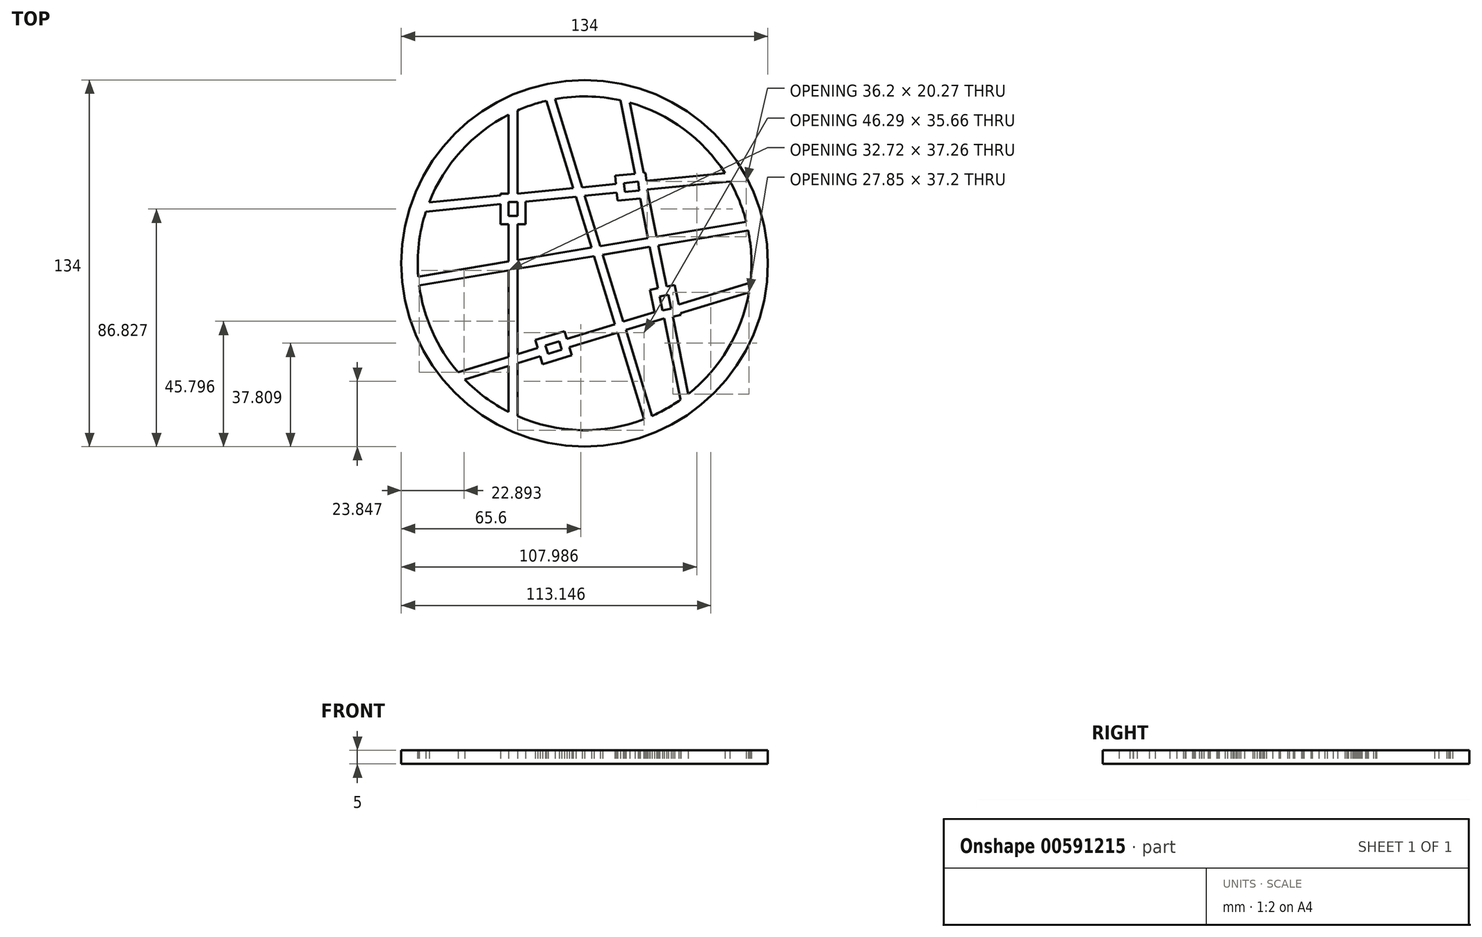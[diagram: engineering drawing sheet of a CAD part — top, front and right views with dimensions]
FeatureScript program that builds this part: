
annotation { "Feature Type Name" : "Feature", "Feature Type Description" : "" }
export const myFeature = defineFeature(function(context is Context, id is Id, definition is map)
    precondition{}
    {
        {
            var Q0;
            Q0=qCreatedBy(makeId("Top.planeOp"),FACE);
            var sketch = newSketch(context, id + "F0", { "sketchPlane" : qUnion([Q0])});
            skCircle(sketch, "E0", {"center": v(0, 0) * mm, "radius": 67 * mm});
            skArc(sketch, "E1.0", {"start": v(51.3, 33) * mm, "mid": v(36.26, 49.05) * mm, "end": v(16.5, 58.73) * mm});
            skLineSegment(sketch, "E2.bottom", {"start": v(-27.75, 22.47) * mm, "end": v(-24.55, 22.47) * mm});
            skLineSegment(sketch, "E2.top", {"start": v(-27.75, 17.27) * mm, "end": v(-24.55, 17.27) * mm});
            skLineSegment(sketch, "E2.left", {"start": v(-27.75, 22.47) * mm, "end": v(-27.75, 17.27) * mm});
            skLineSegment(sketch, "E2.right", {"start": v(-24.55, 22.47) * mm, "end": v(-24.55, 17.27) * mm});
            skLineSegment(sketch, "E3.1.0", {"start": v(19.92, 26.65) * mm, "end": v(14.75, 26.14) * mm});
            skLineSegment(sketch, "E3.1.1", {"start": v(19.6, 29.84) * mm, "end": v(14.43, 29.32) * mm});
            skLineSegment(sketch, "E3.1.2", {"start": v(14.43, 29.32) * mm, "end": v(14.75, 26.14) * mm});
            skLineSegment(sketch, "E3.1.3", {"start": v(19.6, 29.84) * mm, "end": v(19.92, 26.65) * mm});
            skLineSegment(sketch, "E3.2.0", {"start": v(28.5, -17.18) * mm, "end": v(27.47, -12.08) * mm});
            skLineSegment(sketch, "E3.2.1", {"start": v(31.63, -16.55) * mm, "end": v(30.6, -11.45) * mm});
            skLineSegment(sketch, "E3.2.2", {"start": v(30.6, -11.45) * mm, "end": v(27.47, -12.08) * mm});
            skLineSegment(sketch, "E3.2.3", {"start": v(31.63, -16.55) * mm, "end": v(28.5, -17.18) * mm});
            skLineSegment(sketch, "E3.3.0", {"start": v(-14.28, -30.05) * mm, "end": v(-9.3, -28.52) * mm});
            skLineSegment(sketch, "E3.3.1", {"start": v(-13.34, -33.1) * mm, "end": v(-8.37, -31.58) * mm});
            skLineSegment(sketch, "E3.3.2", {"start": v(-8.37, -31.58) * mm, "end": v(-9.3, -28.52) * mm});
            skLineSegment(sketch, "E3.3.3", {"start": v(-13.34, -33.1) * mm, "end": v(-14.28, -30.05) * mm});
            skLineSegment(sketch, "E3.anchor1", {"start": v(0, 0) * mm, "end": v(-24.55, 17.27) * mm, "construction": true});
            skLineSegment(sketch, "E3.anchor2", {"start": v(0, 0) * mm, "end": v(-9.3, -28.52) * mm, "construction": true});
            skLineSegment(sketch, "E4.bottom", {"start": v(85.31, 41.64) * mm, "end": v(88.31, 41.64) * mm});
            skLineSegment(sketch, "E4.top", {"start": v(85.31, -58.36) * mm, "end": v(88.31, -58.36) * mm});
            skLineSegment(sketch, "E4.left", {"start": v(85.31, 41.64) * mm, "end": v(85.31, 36.64) * mm});
            skLineSegment(sketch, "E4.right", {"start": v(88.31, 41.64) * mm, "end": v(88.31, 36.64) * mm});
            skLineSegment(sketch, "E5.bottom", {"start": v(90.31, -58.36) * mm, "end": v(83.31, -58.36) * mm});
            skLineSegment(sketch, "E5.top", {"start": v(90.31, 36.64) * mm, "end": v(88.31, 36.64) * mm});
            skLineSegment(sketch, "E5.left", {"start": v(90.31, -58.36) * mm, "end": v(90.31, -44) * mm});
            skLineSegment(sketch, "E5.right", {"start": v(83.31, -58.36) * mm, "end": v(83.31, -44) * mm});
            skLineSegment(sketch, "E6", {"start": v(90.31, -44) * mm, "end": v(88.31, -44) * mm});
            skLineSegment(sketch, "E7", {"start": v(90.31, -38.8) * mm, "end": v(88.31, -38.8) * mm});
            skLineSegment(sketch, "E8.trimOffspring", {"start": v(90.31, -38.8) * mm, "end": v(90.31, 36.64) * mm});
            skLineSegment(sketch, "E9.trimOffspring", {"start": v(83.31, -38.8) * mm, "end": v(83.31, 36.64) * mm});
            skLineSegment(sketch, "E10.trimOffspring", {"start": v(85.31, -38.8) * mm, "end": v(83.31, -38.8) * mm});
            skLineSegment(sketch, "E11.trimOffspring", {"start": v(85.31, -44) * mm, "end": v(83.31, -44) * mm});
            skLineSegment(sketch, "E12.trimOffspring", {"start": v(88.31, -38.8) * mm, "end": v(88.31, -44) * mm});
            skLineSegment(sketch, "E13.trimOffspring", {"start": v(85.31, -38.8) * mm, "end": v(85.31, -44) * mm});
            skLineSegment(sketch, "E14.trimOffspring", {"start": v(85.31, 36.64) * mm, "end": v(83.31, 36.64) * mm});
            skLineSegment(sketch, "E15", {"start": v(-27.75, 14.27) * mm, "end": v(-27.75, 0.67) * mm});
            skLineSegment(sketch, "E16", {"start": v(-24.55, 14.27) * mm, "end": v(-24.55, 1.2) * mm});
            skLineSegment(sketch, "E17", {"start": v(-27.75, 25.47) * mm, "end": v(-27.75, 54.32) * mm});
            skLineSegment(sketch, "E18", {"start": v(-24.55, 25.44) * mm, "end": v(-24.55, 55.84) * mm});
            skLineSegment(sketch, "E19", {"start": v(22.59, 30.14) * mm, "end": v(51.3, 33) * mm});
            skLineSegment(sketch, "E20", {"start": v(22.88, 26.95) * mm, "end": v(53.14, 29.96) * mm});
            skLineSegment(sketch, "E21", {"start": v(29.08, -20.1) * mm, "end": v(35.07, -49.91) * mm});
            skLineSegment(sketch, "E22", {"start": v(32.22, -19.49) * mm, "end": v(37.9, -47.8) * mm});
            skLineSegment(sketch, "E23", {"start": v(-17.15, -30.93) * mm, "end": v(-24.55, -33.2) * mm});
            skLineSegment(sketch, "E24", {"start": v(-16.2, -33.99) * mm, "end": v(-24.55, -36.54) * mm});
            skLineSegment(sketch, "E25", {"start": v(11.44, 29.03) * mm, "end": v(-0.91, 27.8) * mm});
            skLineSegment(sketch, "E26", {"start": v(11.76, 25.84) * mm, "end": v(0.05, 24.68) * mm});
            skLineSegment(sketch, "E27", {"start": v(26.87, -9.14) * mm, "end": v(23.83, 6.03) * mm});
            skLineSegment(sketch, "E28", {"start": v(30.01, -8.5) * mm, "end": v(26.98, 6.55) * mm});
            skLineSegment(sketch, "E29", {"start": v(-6.44, -27.64) * mm, "end": v(11.1, -22.27) * mm});
            skLineSegment(sketch, "E30", {"start": v(-5.5, -30.7) * mm, "end": v(12.03, -25.33) * mm});
            skLineSegment(sketch, "E31.0", {"start": v(22.3, 33.12) * mm, "end": v(21.66, 33.06) * mm});
            skLineSegment(sketch, "E31.1", {"start": v(22.3, 33.12) * mm, "end": v(22.9, 26.95) * mm});
            skLineSegment(sketch, "E31.2", {"start": v(20.28, 23.67) * mm, "end": v(12.06, 22.86) * mm});
            skLineSegment(sketch, "E31.3", {"start": v(11.15, 32.01) * mm, "end": v(11.44, 29.03) * mm});
            skLineSegment(sketch, "E32.0", {"start": v(-21.55, 22.53) * mm, "end": v(-21.55, 14.27) * mm});
            skLineSegment(sketch, "E32.1", {"start": v(-30.75, 25.47) * mm, "end": v(-27.75, 25.47) * mm});
            skLineSegment(sketch, "E32.2", {"start": v(-30.75, 25.47) * mm, "end": v(-30.75, 24.83) * mm});
            skLineSegment(sketch, "E32.3", {"start": v(-30.75, 14.27) * mm, "end": v(-27.75, 14.27) * mm});
            skLineSegment(sketch, "E33.0", {"start": v(-18.03, -28.06) * mm, "end": v(-7.32, -24.77) * mm});
            skLineSegment(sketch, "E33.1", {"start": v(-15.33, -36.85) * mm, "end": v(-16.2, -33.99) * mm});
            skLineSegment(sketch, "E33.2", {"start": v(-15.33, -36.85) * mm, "end": v(-4.62, -33.57) * mm});
            skLineSegment(sketch, "E33.3", {"start": v(-4.62, -33.57) * mm, "end": v(-5.5, -30.7) * mm});
            skLineSegment(sketch, "E34.0", {"start": v(35.16, -18.9) * mm, "end": v(32.22, -19.49) * mm});
            skLineSegment(sketch, "E34.1", {"start": v(35.16, -18.9) * mm, "end": v(32.95, -7.92) * mm});
            skLineSegment(sketch, "E34.2", {"start": v(32.95, -7.92) * mm, "end": v(30.01, -8.5) * mm});
            skLineSegment(sketch, "E34.3", {"start": v(25.56, -17.83) * mm, "end": v(23.93, -9.73) * mm});
            skLineSegment(sketch, "E35.trimOffspring", {"start": v(26.87, -9.14) * mm, "end": v(23.93, -9.73) * mm});
            skLineSegment(sketch, "E36.trimOffspring", {"start": v(34.4, -15.12) * mm, "end": v(60.59, -7.09) * mm});
            skLineSegment(sketch, "E37.trimOffspring", {"start": v(35.03, -18.27) * mm, "end": v(60.07, -10.6) * mm});
            skLineSegment(sketch, "E38.trimOffspring", {"start": v(-6.44, -27.64) * mm, "end": v(-7.32, -24.77) * mm});
            skLineSegment(sketch, "E39.trimOffspring", {"start": v(-17.15, -30.93) * mm, "end": v(-18.03, -28.06) * mm});
            skLineSegment(sketch, "E40.trimOffspring", {"start": v(-24.55, -36.54) * mm, "end": v(-24.55, -55.84) * mm});
            skLineSegment(sketch, "E41.trimOffspring", {"start": v(-27.75, -34.18) * mm, "end": v(-46.2, -39.84) * mm});
            skLineSegment(sketch, "E42.trimOffspring", {"start": v(-27.75, -37.52) * mm, "end": v(-27.75, -54.32) * mm});
            skLineSegment(sketch, "E43.trimOffspring", {"start": v(-27.75, -37.52) * mm, "end": v(-43.8, -42.45) * mm});
            skLineSegment(sketch, "E44.trimOffspring", {"start": v(-24.55, 14.27) * mm, "end": v(-21.55, 14.27) * mm});
            skLineSegment(sketch, "E45.trimOffspring", {"start": v(-30.75, 21.61) * mm, "end": v(-58, 18.9) * mm});
            skLineSegment(sketch, "E46.trimOffspring", {"start": v(-30.75, 21.61) * mm, "end": v(-30.75, 14.27) * mm});
            skLineSegment(sketch, "E47.trimOffspring", {"start": v(-30.75, 24.83) * mm, "end": v(-56.8, 22.23) * mm});
            skLineSegment(sketch, "E48.trimOffspring", {"start": v(21.66, 33.06) * mm, "end": v(16.5, 58.73) * mm});
            skLineSegment(sketch, "E49.trimOffspring", {"start": v(18.46, 32.74) * mm, "end": v(11.15, 32.01) * mm});
            skLineSegment(sketch, "E50.trimOffspring", {"start": v(18.46, 32.74) * mm, "end": v(13.06, 59.59) * mm});
            skLineSegment(sketch, "E51.trimOffspring", {"start": v(11.76, 25.84) * mm, "end": v(12.06, 22.86) * mm});
            skArc(sketch, "E52.trimOffspring", {"start": v(13.06, 59.59) * mm, "mid": v(1.15, 60.99) * mm, "end": v(-10.8, 60.04) * mm});
            skArc(sketch, "E53.trimOffspring", {"start": v(-27.75, 54.32) * mm, "mid": v(-45.22, 40.94) * mm, "end": v(-56.8, 22.23) * mm});
            skArc(sketch, "E54.trimOffspring", {"start": v(-58, 18.9) * mm, "mid": v(-60.58, 7.17) * mm, "end": v(-60.8, -4.84) * mm});
            skArc(sketch, "E55.trimOffspring", {"start": v(-43.8, -42.45) * mm, "mid": v(-36.27, -49.05) * mm, "end": v(-27.75, -54.32) * mm});
            skArc(sketch, "E56.trimOffspring", {"start": v(-24.55, -55.84) * mm, "mid": v(-1.51, -60.98) * mm, "end": v(21.74, -57) * mm});
            skArc(sketch, "E57.trimOffspring", {"start": v(37.9, -47.8) * mm, "mid": v(52.4, -31.22) * mm, "end": v(60.07, -10.6) * mm});
            skArc(sketch, "E58.trimOffspring", {"start": v(60.59, -7.09) * mm, "mid": v(60.95, 2.5) * mm, "end": v(59.8, 12.03) * mm});
            skLineSegment(sketch, "E59", {"start": v(59.8, 12.03) * mm, "end": v(26.98, 6.55) * mm});
            skPoint(sketch, "E59.endSnap0", {"position": v(-59.8, -12.02) * mm});
            skLineSegment(sketch, "E60.0", {"start": v(59.09, 15.15) * mm, "end": v(26.35, 9.7) * mm});
            skLineSegment(sketch, "E61.trimOffspring", {"start": v(-27.75, 0.67) * mm, "end": v(-60.8, -4.84) * mm});
            skLineSegment(sketch, "E62.trimOffspring", {"start": v(-27.75, -2.57) * mm, "end": v(-59.8, -7.92) * mm});
            skLineSegment(sketch, "E63.trimOffspring", {"start": v(-24.55, -2.04) * mm, "end": v(-24.55, -33.2) * mm});
            skLineSegment(sketch, "E64.trimOffspring", {"start": v(-27.75, -2.57) * mm, "end": v(-27.75, -34.18) * mm});
            skLineSegment(sketch, "E65.trimOffspring", {"start": v(23.2, 9.17) * mm, "end": v(20.28, 23.67) * mm});
            skLineSegment(sketch, "E66.trimOffspring", {"start": v(23.2, 9.17) * mm, "end": v(5.7, 6.25) * mm});
            skLineSegment(sketch, "E67.trimOffspring", {"start": v(26.35, 9.7) * mm, "end": v(22.88, 26.95) * mm});
            skLineSegment(sketch, "E68.trimOffspring", {"start": v(23.83, 6.03) * mm, "end": v(6.64, 3.16) * mm});
            skArc(sketch, "E69.trimOffspring", {"start": v(59.09, 15.15) * mm, "mid": v(56.6, 22.75) * mm, "end": v(53.14, 29.96) * mm});
            skLineSegment(sketch, "E70", {"start": v(-59.8, -7.92) * mm, "end": v(-60.47, -8.03) * mm});
            skArc(sketch, "E71.trimOffspring", {"start": v(-60.47, -8.03) * mm, "mid": v(-55.65, -24.97) * mm, "end": v(-46.2, -39.84) * mm});
            skLineSegment(sketch, "E72", {"start": v(-13.95, 59.38) * mm, "end": v(-4.16, 27.47) * mm});
            skLineSegment(sketch, "E73.0", {"start": v(-10.8, 60.04) * mm, "end": v(-0.91, 27.8) * mm});
            skArc(sketch, "E74.trimOffspring", {"start": v(-13.95, 59.38) * mm, "mid": v(-19.33, 57.86) * mm, "end": v(-24.55, 55.84) * mm});
            skLineSegment(sketch, "E75.trimOffspring", {"start": v(0.05, 24.68) * mm, "end": v(5.7, 6.25) * mm});
            skLineSegment(sketch, "E76.trimOffspring", {"start": v(-4.16, 27.47) * mm, "end": v(-24.55, 25.44) * mm});
            skLineSegment(sketch, "E77.trimOffspring", {"start": v(-3.2, 24.35) * mm, "end": v(2.51, 5.72) * mm});
            skLineSegment(sketch, "E78.trimOffspring", {"start": v(-3.2, 24.35) * mm, "end": v(-21.55, 22.53) * mm});
            skLineSegment(sketch, "E79.trimOffspring", {"start": v(6.64, 3.16) * mm, "end": v(14.15, -21.33) * mm});
            skLineSegment(sketch, "E80.trimOffspring", {"start": v(2.51, 5.72) * mm, "end": v(-24.55, 1.2) * mm});
            skLineSegment(sketch, "E81.trimOffspring", {"start": v(3.46, 2.63) * mm, "end": v(11.1, -22.27) * mm});
            skLineSegment(sketch, "E82.trimOffspring", {"start": v(3.46, 2.63) * mm, "end": v(-24.55, -2.04) * mm});
            skLineSegment(sketch, "E83.trimOffspring", {"start": v(15.1, -24.39) * mm, "end": v(24.72, -55.77) * mm});
            skLineSegment(sketch, "E84.trimOffspring", {"start": v(15.1, -24.39) * mm, "end": v(29.08, -20.1) * mm});
            skLineSegment(sketch, "E85.trimOffspring", {"start": v(14.15, -21.33) * mm, "end": v(25.56, -17.83) * mm});
            skLineSegment(sketch, "E86.trimOffspring", {"start": v(12.03, -25.33) * mm, "end": v(21.74, -57) * mm});
            skArc(sketch, "E87.trimOffspring", {"start": v(24.72, -55.77) * mm, "mid": v(30.04, -53.1) * mm, "end": v(35.07, -49.91) * mm});
            skSolve(sketch);
        }
        {
            var Q0;
            Q0=makeQuery(id+"F0.imprint","IMPRINT",FACE,{"disambiguationData":[TD([[makeQuery(id+"F0.imprint","IMPRINT",EDGE,{"derivedFrom":sQuery(id+"F0.wireOp",EDGE,"E0")}),1.0]])]});
            extrude(context, id + "F1", {"entities" : qUnion([Q0]), "depth" : 5 * mm, "offsetDistance" : 25 * mm});
        }
    });
